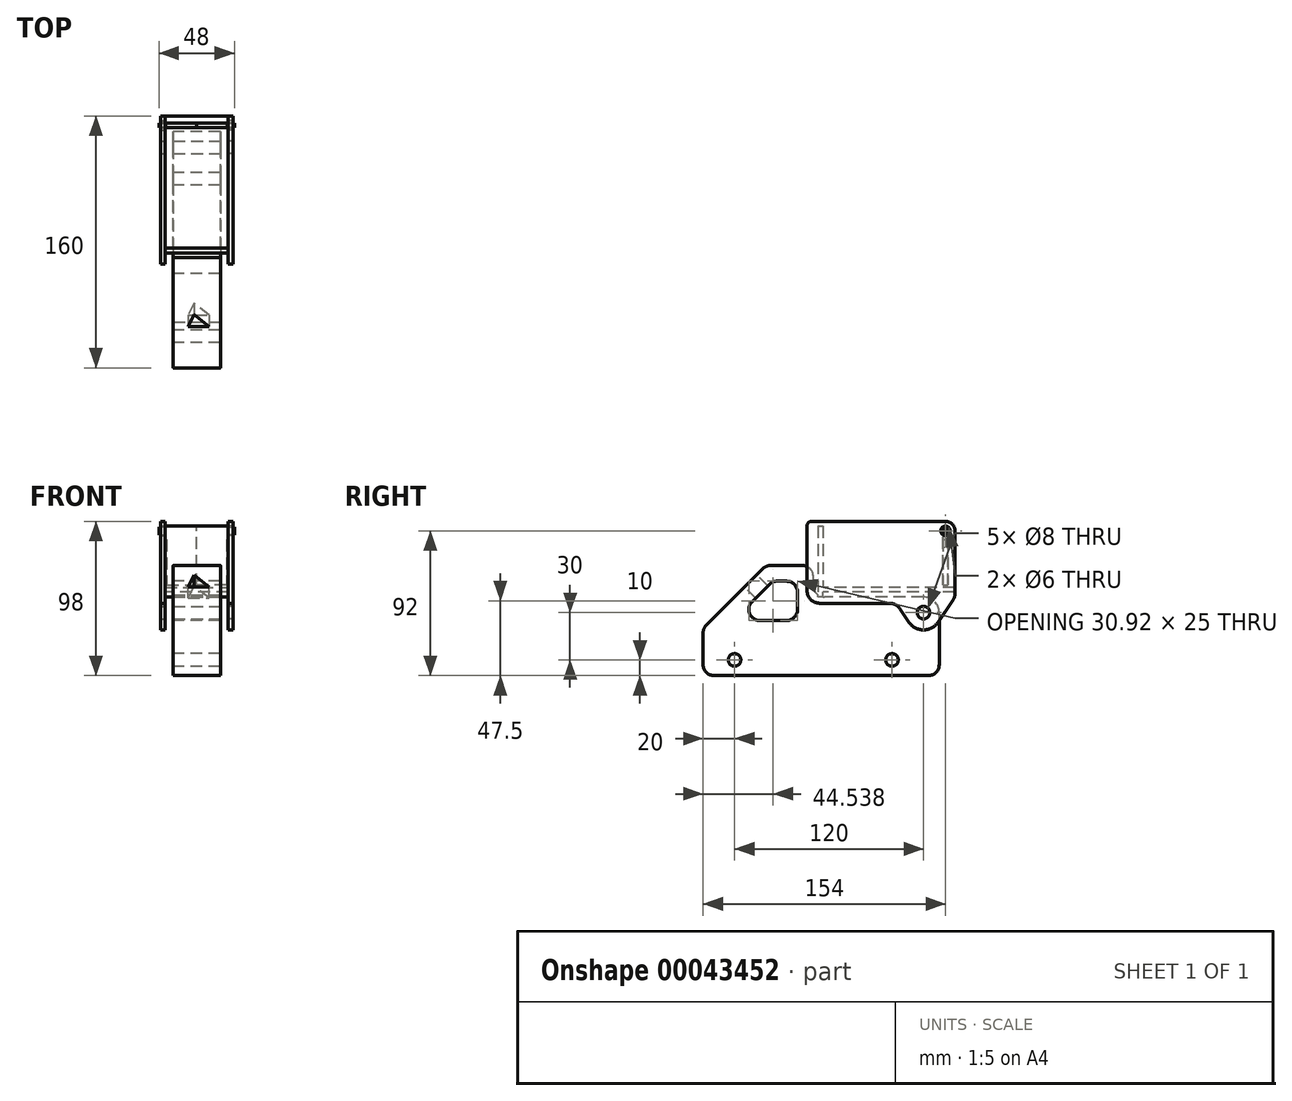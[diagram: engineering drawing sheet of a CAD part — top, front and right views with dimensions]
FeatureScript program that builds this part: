
annotation { "Feature Type Name" : "Feature", "Feature Type Description" : "" }
export const myFeature = defineFeature(function(context is Context, id is Id, definition is map)
    precondition{}
    {
        {
            var Q0;
            Q0=qCreatedBy(makeId("Right.planeOp"),FACE);
            var sketch = newSketch(context, id + "F0", { "sketchPlane" : qUnion([Q0])});
            skLineSegment(sketch, "E0", {"start": v(0, 0) * mm, "end": v(150, 0) * mm});
            skLineSegment(sketch, "E1", {"start": v(150, 0) * mm, "end": v(150, 50) * mm});
            skLineSegment(sketch, "E2", {"start": v(150, 50) * mm, "end": v(70, 50) * mm});
            skLineSegment(sketch, "E3", {"start": v(70, 50) * mm, "end": v(70, 70) * mm});
            skLineSegment(sketch, "E4", {"start": v(70, 70) * mm, "end": v(40, 70) * mm});
            skLineSegment(sketch, "E5", {"start": v(40, 70) * mm, "end": v(0, 30) * mm});
            skLineSegment(sketch, "E6", {"start": v(0, 30) * mm, "end": v(0, 0) * mm});
            skLineSegment(sketch, "E7.0", {"start": v(44.14, 60) * mm, "end": v(19.14, 35) * mm});
            skLineSegment(sketch, "E7.1", {"start": v(60, 60) * mm, "end": v(44.14, 60) * mm});
            skLineSegment(sketch, "E7.2", {"start": v(60, 35) * mm, "end": v(60, 60) * mm});
            skLineSegment(sketch, "E8", {"start": v(19.14, 35) * mm, "end": v(60, 35) * mm});
            skCircle(sketch, "E9", {"center": v(20, 10) * mm, "radius": 4 * mm});
            skCircle(sketch, "E10", {"center": v(120, 10) * mm, "radius": 4 * mm});
            skSolve(sketch);
        }
        {
            var Q0;
            Q0=makeQuery(id+"F0.imprint","IMPRINT",FACE,{"disambiguationData":[TD([[makeQuery(id+"F0.imprint","IMPRINT",EDGE,{"derivedFrom":sQuery(id+"F0.wireOp",EDGE,"E0")}),1.0]])]});
            extrude(context, id + "F1", {"entities" : qUnion([Q0]), "endBound" : BoundingType.SYMMETRIC, "depth" : 30 * mm});
        }
        {
            var Q0;
            Q0=makeQuery(id+"F1.opExtrude","SWEPT_EDGE",EDGE,{"disambiguationData":[OSD([sQuery(id+"F0.wireOp",EDGE,"E4"),sQuery(id+"F0.wireOp",EDGE,"E5")])]});
            var Q1;
            Q1=makeQuery(id+"F1.opExtrude","SWEPT_EDGE",EDGE,{"disambiguationData":[OSD([sQuery(id+"F0.wireOp",EDGE,"E3"),sQuery(id+"F0.wireOp",EDGE,"E4")])]});
            var Q2;
            Q2=makeQuery(id+"F1.opExtrude","SWEPT_EDGE",EDGE,{"disambiguationData":[OSD([sQuery(id+"F0.wireOp",EDGE,"E5"),sQuery(id+"F0.wireOp",EDGE,"E6")])]});
            var Q3;
            Q3=makeQuery(id+"F1.opExtrude","SWEPT_EDGE",EDGE,{"disambiguationData":[OSD([sQuery(id+"F0.wireOp",EDGE,"E0"),sQuery(id+"F0.wireOp",EDGE,"E6")])]});
            var Q4;
            Q4=makeQuery(id+"F1.opExtrude","SWEPT_EDGE",EDGE,{"disambiguationData":[OSD([sQuery(id+"F0.wireOp",EDGE,"E0"),sQuery(id+"F0.wireOp",EDGE,"E1")])]});
            var Q5;
            Q5=makeQuery(id+"F1.opExtrude","SWEPT_EDGE",EDGE,{"disambiguationData":[OSD([sQuery(id+"F0.wireOp",EDGE,"E7.2"),sQuery(id+"F0.wireOp",EDGE,"E8")])]});
            var Q6;
            Q6=makeQuery(id+"F1.opExtrude","SWEPT_EDGE",EDGE,{"disambiguationData":[OSD([sQuery(id+"F0.wireOp",EDGE,"E7.0"),sQuery(id+"F0.wireOp",EDGE,"E7.1")])]});
            var Q7;
            Q7=makeQuery(id+"F1.opExtrude","SWEPT_EDGE",EDGE,{"disambiguationData":[OSD([sQuery(id+"F0.wireOp",EDGE,"E7.0"),sQuery(id+"F0.wireOp",EDGE,"E8")])]});
            var Q8;
            Q8=makeQuery(id+"F1.opExtrude","SWEPT_EDGE",EDGE,{"disambiguationData":[OSD([sQuery(id+"F0.wireOp",EDGE,"E7.1"),sQuery(id+"F0.wireOp",EDGE,"E7.2")])]});
            var Q9;
            Q9=makeQuery(id+"F1.opExtrude","SWEPT_EDGE",EDGE,{"disambiguationData":[OSD([sQuery(id+"F0.wireOp",EDGE,"E2"),sQuery(id+"F0.wireOp",EDGE,"E3")])]});
            fillet(context, id + "F2", {"entities" : qUnion([Q0, Q1, Q2, Q3, Q4, Q5, Q6, Q7, Q8, Q9]), "radius" : 7 * mm, "tangentPropagation" : true, "allowEdgeOverflow" : false});
        }
        {
            var Q0;
            Q0=makeQuery(id+"F1.opExtrude","SWEPT_FACE",FACE,{"disambiguationData":[OSD([sQuery(id+"F0.wireOp",EDGE,"E5")])]});
            var sketch = newSketch(context, id + "F3", { "sketchPlane" : qUnion([Q0])});
            skLineSegment(sketch, "E11", {"start": v(-1.78, 69.3) * mm, "end": v(-5.5, 58.43) * mm});
            skLineSegment(sketch, "E12", {"start": v(-5.5, 58.43) * mm, "end": v(7.93, 58.43) * mm});
            skLineSegment(sketch, "E13", {"start": v(7.93, 58.43) * mm, "end": v(-1.78, 69.3) * mm});
            skSolve(sketch);
        }
        {
            var Q0;
            Q0=qSketchRegion(id+"F3",true);
            extrude(context, id + "F4", {"entities" : qUnion([Q0]), "operationType" : NewBodyOperationType.REMOVE, "endBound" : BoundingType.UP_TO_NEXT, "oppositeDirection" : true, "depth" : 17.54 * mm});
        }
        {
            var Q0;
            Q0=makeQuery(id+"F1.opExtrude","SWEPT_EDGE",EDGE,{"disambiguationData":[OSD([sQuery(id+"F0.wireOp",EDGE,"E1"),sQuery(id+"F0.wireOp",EDGE,"E2")])]});
            fillet(context, id + "F5", {"entities" : qUnion([Q0]), "radius" : 10 * mm, "tangentPropagation" : true, "allowEdgeOverflow" : false});
        }
        {
            var Q0;
            Q0=qCreatedBy(makeId("Right.planeOp"),FACE);
            var sketch = newSketch(context, id + "F6", { "sketchPlane" : qUnion([Q0])});
            skCircle(sketch, "E14", {"center": v(140, 40) * mm, "radius": 4 * mm});
            skSolve(sketch);
        }
        {
            var Q0;
            Q0=qSketchRegion(id+"F6",true);
            extrude(context, id + "F7", {"entities" : qUnion([Q0]), "operationType" : NewBodyOperationType.REMOVE, "endBound" : BoundingType.SYMMETRIC, "oppositeDirection" : true, "depth" : 110.99 * mm});
        }
        {
            var Q0;
            Q0=makeQuery(id+"F1.opExtrude","CAP_FACE",FACE,{"disambiguationData":[OSD([sQuery(id+"F0.wireOp",EDGE,"E0"),sQuery(id+"F0.wireOp",EDGE,"E1"),sQuery(id+"F0.wireOp",EDGE,"E2"),sQuery(id+"F0.wireOp",EDGE,"E3"),sQuery(id+"F0.wireOp",EDGE,"E4"),sQuery(id+"F0.wireOp",EDGE,"E5"),sQuery(id+"F0.wireOp",EDGE,"E6"),sQuery(id+"F0.wireOp",EDGE,"E7.0"),sQuery(id+"F0.wireOp",EDGE,"E7.1"),sQuery(id+"F0.wireOp",EDGE,"E7.2"),sQuery(id+"F0.wireOp",EDGE,"E8"),sQuery(id+"F0.wireOp",EDGE,"E9"),sQuery(id+"F0.wireOp",EDGE,"E10")])],"isStart":false});
            cPlane(context, id + "F8", {"entities" : qUnion([Q0]), "cplaneType" : CPlaneType.OFFSET, "offset" : 5 * mm, "width" : 150 * mm, "height" : 150 * mm});
        }
        {
            var Q0;
            Q0=qCreatedBy(id+"F8.planeOp",FACE);
            var sketch = newSketch(context, id + "F9", { "sketchPlane" : qUnion([Q0])});
            skLineSegment(sketch, "E15.bottom", {"start": v(69, 98) * mm, "end": v(154, 98) * mm});
            skLineSegment(sketch, "E15.top", {"start": v(74, 46) * mm, "end": v(118.44, 46) * mm});
            skLineSegment(sketch, "E15.left", {"start": v(66, 95) * mm, "end": v(66, 54) * mm});
            skLineSegment(sketch, "E15.right", {"start": v(160, 92) * mm, "end": v(160, 56) * mm});
            skArc(sketch, "E16", {"start": v(130.88, 33.85) * mm, "mid": v(140, 29) * mm, "end": v(149.12, 33.85) * mm});
            skLineSegment(sketch, "E17", {"start": v(158.98, 48.48) * mm, "end": v(149.12, 33.85) * mm});
            skLineSegment(sketch, "E18", {"start": v(125.07, 42.47) * mm, "end": v(130.88, 33.85) * mm});
            skLineSegment(sketch, "E19", {"start": v(140, 40) * mm, "end": v(140, 71.93) * mm, "construction": true});
            skCircle(sketch, "E20.0", {"center": v(140, 40) * mm, "radius": 4 * mm});
            skLineSegment(sketch, "E21.bottom", {"start": v(73, 84) * mm, "end": v(76, 84) * mm});
            skLineSegment(sketch, "E21.top", {"start": v(73, 64) * mm, "end": v(76, 64) * mm});
            skLineSegment(sketch, "E21.left", {"start": v(73, 84) * mm, "end": v(73, 64) * mm});
            skLineSegment(sketch, "E21.right", {"start": v(76, 84) * mm, "end": v(76, 64) * mm});
            skLineSegment(sketch, "E22.bottom", {"start": v(160, 56) * mm, "end": v(140, 56) * mm});
            skLineSegment(sketch, "E22.top", {"start": v(160, 53) * mm, "end": v(140, 53) * mm});
            skLineSegment(sketch, "E22.right", {"start": v(140, 56) * mm, "end": v(140, 53) * mm});
            skLineSegment(sketch, "E23.trimOffspring", {"start": v(160, 53) * mm, "end": v(160, 51.83) * mm});
            skPoint(sketch, "E24.visualSharp", {"position": v(160, 98) * mm});
            skArc(sketch, "E24.filletArc", {"start": v(160, 92) * mm, "mid": v(158.24, 96.24) * mm, "end": v(154, 98) * mm});
            skPoint(sketch, "E25.visualSharp", {"position": v(66, 98) * mm});
            skArc(sketch, "E25.filletArc", {"start": v(69, 98) * mm, "mid": v(66.88, 97.12) * mm, "end": v(66, 95) * mm});
            skPoint(sketch, "E26.visualSharp", {"position": v(66, 46) * mm});
            skArc(sketch, "E26.filletArc", {"start": v(66, 54) * mm, "mid": v(68.34, 48.34) * mm, "end": v(74, 46) * mm});
            skPoint(sketch, "E27.visualSharp", {"position": v(160, 50) * mm});
            skArc(sketch, "E27.filletArc", {"start": v(158.98, 48.48) * mm, "mid": v(159.74, 50.08) * mm, "end": v(160, 51.83) * mm});
            skCircle(sketch, "E28", {"center": v(154, 92) * mm, "radius": 3 * mm});
            skPoint(sketch, "E29.visualSharp", {"position": v(122.7, 46) * mm});
            skArc(sketch, "E29.filletArc", {"start": v(125.07, 42.47) * mm, "mid": v(122.2, 45.06) * mm, "end": v(118.44, 46) * mm});
            skSolve(sketch);
        }
        {
            var Q0;
            Q0=qSketchRegion(id+"F9",true);
            extrude(context, id + "F10", {"entities" : qUnion([Q0]), "depth" : 3 * mm});
        }
        {
            var Q0;
            Q0=makeQuery(id+"F10.opExtrude","SWEPT_BODY",BODY,{"disambiguationData":[OSD([sQuery(id+"F9.wireOp",EDGE,"E15.bottom"),sQuery(id+"F9.wireOp",EDGE,"E15.top"),sQuery(id+"F9.wireOp",EDGE,"E15.left"),sQuery(id+"F9.wireOp",EDGE,"E15.right"),sQuery(id+"F9.wireOp",EDGE,"E16"),sQuery(id+"F9.wireOp",EDGE,"E17"),sQuery(id+"F9.wireOp",EDGE,"E18"),sQuery(id+"F9.wireOp",EDGE,"E20.0"),sQuery(id+"F9.wireOp",EDGE,"E21.bottom"),sQuery(id+"F9.wireOp",EDGE,"E21.top"),sQuery(id+"F9.wireOp",EDGE,"E21.left"),sQuery(id+"F9.wireOp",EDGE,"E21.right"),sQuery(id+"F9.wireOp",EDGE,"E22.bottom"),sQuery(id+"F9.wireOp",EDGE,"E22.top"),sQuery(id+"F9.wireOp",EDGE,"E22.right"),sQuery(id+"F9.wireOp",EDGE,"E23.trimOffspring"),sQuery(id+"F9.wireOp",EDGE,"E24.filletArc"),sQuery(id+"F9.wireOp",EDGE,"E25.filletArc"),sQuery(id+"F9.wireOp",EDGE,"E26.filletArc"),sQuery(id+"F9.wireOp",EDGE,"E27.filletArc"),sQuery(id+"F9.wireOp",EDGE,"E28")])]});
            var Q1;
            Q1=qCreatedBy(makeId("Right.planeOp"),FACE);
            mirror(context, id + "F11", {"entities" : qUnion([Q0]), "mirrorPlane" : qUnion([Q1])});
        }
        {
            var Q0;
            Q0=makeQuery(id+"F10.opExtrude","SWEPT_FACE",FACE,{"disambiguationData":[OSD([sQuery(id+"F9.wireOp",EDGE,"E22.top")])]});
            var sketch = newSketch(context, id + "F12", { "sketchPlane" : qUnion([Q0])});
            skLineSegment(sketch, "E30.bottom", {"start": v(20, 76) * mm, "end": v(8, 76) * mm});
            skLineSegment(sketch, "E30.top", {"start": v(20, 160) * mm, "end": v(0, 160) * mm});
            skLineSegment(sketch, "E30.left", {"start": v(20, 76) * mm, "end": v(20, 140) * mm});
            skLineSegment(sketch, "E30.right", {"start": v(0, 76) * mm, "end": v(0, 160) * mm});
            skLineSegment(sketch, "E31", {"start": v(20, 160) * mm, "end": v(23, 160) * mm});
            skLineSegment(sketch, "E32", {"start": v(23, 160) * mm, "end": v(23, 140) * mm});
            skLineSegment(sketch, "E33", {"start": v(23, 140) * mm, "end": v(20, 140) * mm});
            skLineSegment(sketch, "E34", {"start": v(0, 76) * mm, "end": v(0, 73) * mm});
            skLineSegment(sketch, "E35", {"start": v(0, 73) * mm, "end": v(8, 73) * mm});
            skLineSegment(sketch, "E36", {"start": v(8, 73) * mm, "end": v(8, 76) * mm});
            skSolve(sketch);
        }
        {
            var Q0;
            Q0=qSketchRegion(id+"F12",true);
            extrude(context, id + "F13", {"entities" : qUnion([Q0]), "depth" : 3 * mm});
        }
        {
            var Q0;
            Q0=makeQuery(id+"F13.opExtrude","SWEPT_BODY",BODY,{"disambiguationData":[OSD([sQuery(id+"F12.wireOp",EDGE,"E30.bottom"),sQuery(id+"F12.wireOp",EDGE,"E30.top"),sQuery(id+"F12.wireOp",EDGE,"E30.left"),sQuery(id+"F12.wireOp",EDGE,"E30.right"),sQuery(id+"F12.wireOp",EDGE,"E31"),sQuery(id+"F12.wireOp",EDGE,"E32"),sQuery(id+"F12.wireOp",EDGE,"E33")])]});
            var Q1;
            Q1=makeQuery(id+"F13.opExtrude","SWEPT_FACE",FACE,{"disambiguationData":[OSD([sQuery(id+"F12.wireOp",EDGE,"E30.right")])]});
            mirror(context, id + "F14", {"operationType" : NewBodyOperationType.ADD, "entities" : qUnion([Q0]), "mirrorPlane" : qUnion([Q1])});
        }
        {
            var Q0;
            Q0=makeQuery(id+"F10.opExtrude","SWEPT_FACE",FACE,{"disambiguationData":[OSD([sQuery(id+"F9.wireOp",EDGE,"E21.right")])]});
            var sketch = newSketch(context, id + "F15", { "sketchPlane" : qUnion([Q0])});
            skLineSegment(sketch, "E37", {"start": v(20, 64) * mm, "end": v(23, 64) * mm});
            skLineSegment(sketch, "E38", {"start": v(23, 64) * mm, "end": v(23, 84) * mm});
            skLineSegment(sketch, "E39", {"start": v(23, 84) * mm, "end": v(20, 84) * mm});
            skLineSegment(sketch, "E40", {"start": v(20, 84) * mm, "end": v(20, 95) * mm});
            skLineSegment(sketch, "E41", {"start": v(20, 95) * mm, "end": v(0, 95) * mm});
            skLineSegment(sketch, "E42", {"start": v(0, 95) * mm, "end": v(0, 56) * mm});
            skLineSegment(sketch, "E43", {"start": v(0, 50) * mm, "end": v(20, 50) * mm});
            skLineSegment(sketch, "E44", {"start": v(20, 50) * mm, "end": v(20, 64) * mm});
            skLineSegment(sketch, "E45.0", {"start": v(0, 56) * mm, "end": v(8, 56) * mm});
            skLineSegment(sketch, "E46.0", {"start": v(0, 53) * mm, "end": v(8, 53) * mm});
            skLineSegment(sketch, "E47.0", {"start": v(8, 56) * mm, "end": v(8, 53) * mm});
            skPoint(sketch, "E48.orphan", {"position": v(-8, 56) * mm});
            skPoint(sketch, "E49.orphan", {"position": v(-8, 53) * mm});
            skLineSegment(sketch, "E50.trimOffspring", {"start": v(0, 53) * mm, "end": v(0, 50) * mm});
            skSolve(sketch);
        }
        {
            var Q0;
            Q0=qSketchRegion(id+"F15",true);
            extrude(context, id + "F16", {"entities" : qUnion([Q0]), "depth" : 3 * mm});
        }
        {
            var Q0;
            Q0=makeQuery(id+"F16.opExtrude","SWEPT_BODY",BODY,{"disambiguationData":[OSD([sQuery(id+"F15.wireOp",EDGE,"E37"),sQuery(id+"F15.wireOp",EDGE,"E38"),sQuery(id+"F15.wireOp",EDGE,"E39"),sQuery(id+"F15.wireOp",EDGE,"E40"),sQuery(id+"F15.wireOp",EDGE,"E41"),sQuery(id+"F15.wireOp",EDGE,"E42"),sQuery(id+"F15.wireOp",EDGE,"E43"),sQuery(id+"F15.wireOp",EDGE,"E44"),sQuery(id+"F15.wireOp",EDGE,"E45.0"),sQuery(id+"F15.wireOp",EDGE,"E46.0"),sQuery(id+"F15.wireOp",EDGE,"E47.0"),sQuery(id+"F15.wireOp",EDGE,"E50.trimOffspring")])]});
            var Q1;
            Q1=makeQuery(id+"F16.opExtrude","SWEPT_FACE",FACE,{"disambiguationData":[OSD([sQuery(id+"F15.wireOp",EDGE,"E42")])]});
            mirror(context, id + "F17", {"operationType" : NewBodyOperationType.ADD, "entities" : qUnion([Q0]), "mirrorPlane" : qUnion([Q1])});
        }
        {
            var Q0;
            Q0=makeQuery(id+"F10.opExtrude","CAP_VERTEX",VERTEX,{"disambiguationData":[OSD([sQuery(id+"F9.wireOp",EDGE,"E15.bottom"),sQuery(id+"F9.wireOp",EDGE,"E24.filletArc")])],"isStart":false});
            var Q1;
            Q1=qCreatedBy(makeId("Front.planeOp"),FACE);
            cPlane(context, id + "F18", {"entities" : qUnion([Q0, Q1]), "cplaneType" : CPlaneType.PLANE_POINT, "offset" : 150 * mm, "width" : 150 * mm, "height" : 150 * mm});
        }
        {
            var Q0;
            Q0=qCreatedBy(id+"F18.planeOp",FACE);
            var sketch = newSketch(context, id + "F19", { "sketchPlane" : qUnion([Q0])});
            skLineSegment(sketch, "E51", {"start": v(0, 95) * mm, "end": v(19.7, 95) * mm});
            skLineSegment(sketch, "E52", {"start": v(19.7, 95) * mm, "end": v(19.7, 94.5) * mm});
            skLineSegment(sketch, "E53", {"start": v(19.7, 94.5) * mm, "end": v(24, 94.5) * mm});
            skLineSegment(sketch, "E54", {"start": v(24, 94.5) * mm, "end": v(24, 89.5) * mm});
            skLineSegment(sketch, "E55", {"start": v(24, 89.5) * mm, "end": v(19.7, 89.5) * mm});
            skLineSegment(sketch, "E56", {"start": v(19.7, 89.5) * mm, "end": v(19.7, 86.5) * mm});
            skLineSegment(sketch, "E57", {"start": v(19.7, 86.5) * mm, "end": v(19, 86.5) * mm});
            skLineSegment(sketch, "E58", {"start": v(19, 86.5) * mm, "end": v(19, 57.5) * mm});
            skLineSegment(sketch, "E59", {"start": v(19, 57.5) * mm, "end": v(0, 57.5) * mm});
            skLineSegment(sketch, "E60", {"start": v(0, 57.5) * mm, "end": v(0, 95) * mm});
            skLineSegment(sketch, "E61", {"start": v(49.74, 92) * mm, "end": v(23, 92) * mm, "construction": true});
            skSolve(sketch);
        }
        {
            var Q0;
            Q0=qSketchRegion(id+"F19",true);
            extrude(context, id + "F20", {"entities" : qUnion([Q0]), "endBound" : BoundingType.SYMMETRIC, "depth" : 3 * mm});
        }
        {
            var Q0;
            Q0=makeQuery(id+"F20.opExtrude","SWEPT_BODY",BODY,{"disambiguationData":[OSD([sQuery(id+"F19.wireOp",EDGE,"E51"),sQuery(id+"F19.wireOp",EDGE,"E52"),sQuery(id+"F19.wireOp",EDGE,"E53"),sQuery(id+"F19.wireOp",EDGE,"E54"),sQuery(id+"F19.wireOp",EDGE,"E55"),sQuery(id+"F19.wireOp",EDGE,"E56"),sQuery(id+"F19.wireOp",EDGE,"E57"),sQuery(id+"F19.wireOp",EDGE,"E58"),sQuery(id+"F19.wireOp",EDGE,"E59"),sQuery(id+"F19.wireOp",EDGE,"E60")])]});
            var Q1;
            Q1=makeQuery(id+"F20.opExtrude","SWEPT_FACE",FACE,{"disambiguationData":[OSD([sQuery(id+"F19.wireOp",EDGE,"E60")])]});
            mirror(context, id + "F21", {"operationType" : NewBodyOperationType.ADD, "entities" : qUnion([Q0]), "mirrorPlane" : qUnion([Q1])});
        }
    });
